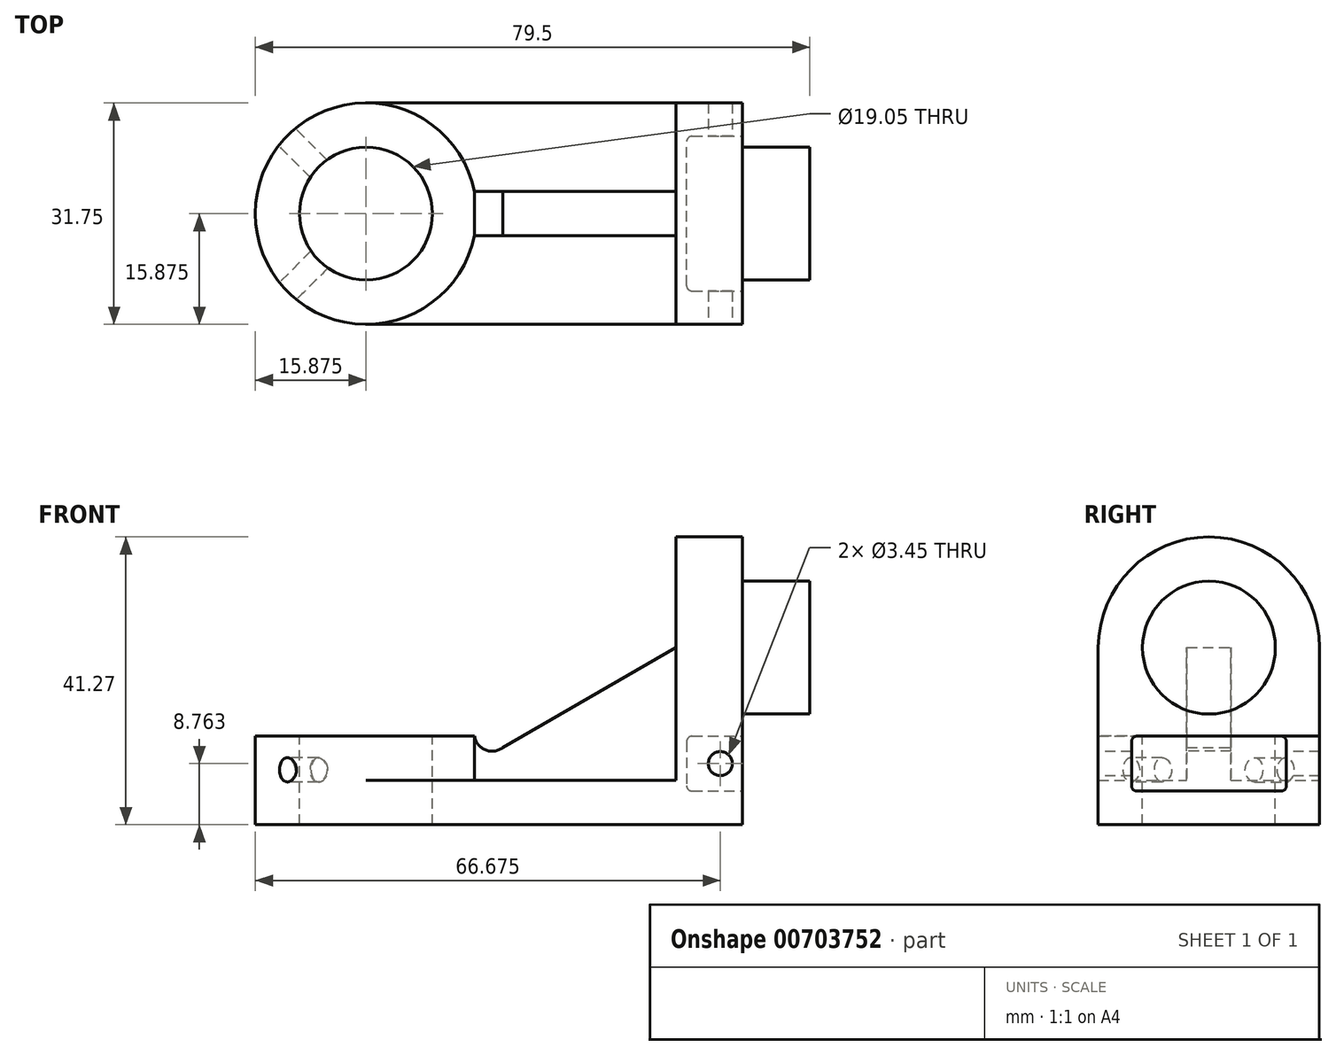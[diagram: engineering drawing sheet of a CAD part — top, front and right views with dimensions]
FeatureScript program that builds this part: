
annotation { "Feature Type Name" : "Feature", "Feature Type Description" : "" }
export const myFeature = defineFeature(function(context is Context, id is Id, definition is map)
    precondition{}
    {
        {
            var Q0;
            Q0=qCreatedBy(makeId("Top.planeOp"),FACE);
            var sketch = newSketch(context, id + "F0", { "sketchPlane" : qUnion([Q0])});
            skLineSegment(sketch, "E0.bottom", {"start": v(0, 0) * mm, "end": v(-53.98, 0) * mm});
            skLineSegment(sketch, "E0.top", {"start": v(0, -31.75) * mm, "end": v(-53.97, -31.75) * mm});
            skLineSegment(sketch, "E0.left", {"start": v(0, 0) * mm, "end": v(0, -31.75) * mm});
            skLineSegment(sketch, "E0.right", {"start": v(-53.98, 0) * mm, "end": v(-53.97, -31.75) * mm});
            skSolve(sketch);
        }
        {
            var Q0;
            Q0 = qSketchRegion(id + "F0", true);
            extrude(context, id + "F1", {"entities" : qUnion([Q0]), "depth" : 6.35 * mm, "offsetDistance" : 25.4 * mm});
        }
        {
            var Q0;
            Q0=makeQuery(id+"F1.opExtrude","CAP_FACE",FACE,{"disambiguationData":[OSD([sQuery(id+"F0.wireOp",EDGE,"E0.bottom"),sQuery(id+"F0.wireOp",EDGE,"E0.top"),sQuery(id+"F0.wireOp",EDGE,"E0.left"),sQuery(id+"F0.wireOp",EDGE,"E0.right")])],"isStart":false});
            var sketch = newSketch(context, id + "F2", { "sketchPlane" : qUnion([Q0])});
            skCircle(sketch, "E1", {"center": v(-53.98, -15.88) * mm, "radius": 15.88 * mm});
            skSolve(sketch);
        }
        {
            var Q0;
            Q0 = qSketchRegion(id + "F2", true);
            extrude(context, id + "F3", {"entities" : qUnion([Q0]), "operationType" : NewBodyOperationType.ADD, "depth" : 6.35 * mm, "offsetDistance" : 25.4 * mm, "hasSecondDirection" : true, "secondDirectionOppositeDirection" : true, "secondDirectionDepth" : 6.35 * mm});
        }
        {
            var Q0;
            Q0=makeQuery(id+"F3.opExtrude","CAP_FACE",FACE,{"disambiguationData":[OSD([sQuery(id+"F2.wireOp",EDGE,"E1")])],"isStart":false});
            var sketch = newSketch(context, id + "F4", { "sketchPlane" : qUnion([Q0])});
            skCircle(sketch, "E2", {"center": v(-53.98, -15.88) * mm, "radius": 9.53 * mm});
            skSolve(sketch);
        }
        {
            var Q0;
            Q0 = qSketchRegion(id + "F4", true);
            extrude(context, id + "F5", {"entities" : qUnion([Q0]), "operationType" : NewBodyOperationType.REMOVE, "oppositeDirection" : true, "depth" : 25.4 * mm, "offsetDistance" : 25.4 * mm});
        }
        {
            var Q0;
            Q0=makeQuery(id+"F1.opExtrude","SWEPT_FACE",FACE,{"disambiguationData":[OSD([sQuery(id+"F0.wireOp",EDGE,"E0.left")])]});
            var sketch = newSketch(context, id + "F6", { "sketchPlane" : qUnion([Q0])});
            skCircle(sketch, "E3", {"center": v(-15.88, 25.4) * mm, "radius": 9.53 * mm});
            skPoint(sketch, "E3.centerSnap0", {"position": v(-15.88, 6.35) * mm});
            skCircle(sketch, "E4", {"center": v(-15.88, 25.4) * mm, "radius": 15.88 * mm});
            skLineSegment(sketch, "E5", {"start": v(0, 0) * mm, "end": v(0, 25.4) * mm});
            skPoint(sketch, "E5.endSnap0", {"position": v(0, 3.18) * mm});
            skLineSegment(sketch, "E6", {"start": v(-31.75, 0) * mm, "end": v(-31.75, 25.4) * mm});
            skLineSegment(sketch, "E7", {"start": v(-31.75, 0) * mm, "end": v(0, 0) * mm});
            skSolve(sketch);
        }
        {
            var Q0;
            {var subQ5=makeQuery(id+"F1.opExtrude","CAP_EDGE",EDGE,{"disambiguationData":[OSD([sQuery(id+"F0.wireOp",EDGE,"E0.left")])],"isStart":false});Q0=makeQuery(id+"F6.imprint","IMPRINT",FACE,{"disambiguationData":[TD([[makeQuery(id+"F6.imprint","IMPRINT",EDGE,{"derivedFrom":subQ5}),-1.0]])]});}
            var Q1;
            {var subQ0=sQuery(id+"F6.wireOp",EDGE,"E7");Q1=makeQuery(id+"F6.imprint","IMPRINT",FACE,{"disambiguationData":[TD([[makeQuery(id+"F6.imprint","IMPRINT",EDGE,{"derivedFrom":subQ0}),-1.0]])]});}
            var Q2;
            Q2=makeQuery(id+"F6.imprint","IMPRINT",FACE,{"disambiguationData":[TD([[makeQuery(id+"F6.imprint","IMPRINT",EDGE,{"derivedFrom":sQuery(id+"F6.wireOp",EDGE,"E3")}),-1.0]])]});
            extrude(context, id + "F7", {"entities" : qUnion([Q0, Q1, Q2]), "operationType" : NewBodyOperationType.ADD, "oppositeDirection" : true, "depth" : 9.52 * mm, "offsetDistance" : 25.4 * mm});
        }
        {
            var Q0;
            Q0=makeQuery(id+"F7.boolean.opBoolean","MERGE",FACE,{"derivedFrom":[makeQuery(id+"F1.opExtrude","SWEPT_FACE",FACE,{"disambiguationData":[OSD([sQuery(id+"F0.wireOp",EDGE,"E0.left")])]}),makeQuery(id+"F7.opExtrude","CAP_FACE",FACE,{"disambiguationData":[OSD([sQuery(id+"F6.wireOp",EDGE,"E3"),sQuery(id+"F6.wireOp",EDGE,"E4"),sQuery(id+"F6.wireOp",EDGE,"E5"),sQuery(id+"F6.wireOp",EDGE,"E6"),sQuery(id+"F6.wireOp",EDGE,"E7")])],"isStart":true})]});
            var sketch = newSketch(context, id + "F8", { "sketchPlane" : qUnion([Q0])});
            skCircle(sketch, "E8", {"center": v(-15.88, 25.4) * mm, "radius": 9.53 * mm});
            skSolve(sketch);
        }
        {
            var Q0;
            Q0=makeQuery(id+"F8.imprint","IMPRINT",FACE,{"disambiguationData":[TD([[makeQuery(id+"F8.imprint","IMPRINT",EDGE,{"derivedFrom":sQuery(id+"F8.wireOp",EDGE,"E8")}),1.0]])]});
            extrude(context, id + "F9", {"entities" : qUnion([Q0]), "operationType" : NewBodyOperationType.ADD, "depth" : 9.65 * mm, "offsetDistance" : 25.4 * mm, "hasSecondDirection" : true, "secondDirectionOppositeDirection" : true, "secondDirectionDepth" : 9.52 * mm});
        }
        {
            var Q0;
            Q0=qCreatedBy(makeId("Front.planeOp"),FACE);
            cPlane(context, id + "F10", {"entities" : qUnion([Q0]), "cplaneType" : CPlaneType.OFFSET, "offset" : 15.88 * mm, "width" : 152.4 * mm, "height" : 152.4 * mm});
        }
        {
            var Q0;
            Q0=qCreatedBy(id+"F10.planeOp",FACE);
            var sketch = newSketch(context, id + "F11", { "sketchPlane" : qUnion([Q0])});
            skLineSegment(sketch, "E9", {"start": v(-9.52, 25.4) * mm, "end": v(-34.38, 11.05) * mm});
            skLineSegment(sketch, "E10", {"start": v(-34.38, 11.05) * mm, "end": v(-34.38, 12.7) * mm});
            skLineSegment(sketch, "E11", {"start": v(-34.38, 12.7) * mm, "end": v(-38.95, 12.7) * mm});
            skLineSegment(sketch, "E12", {"start": v(-38.95, 12.7) * mm, "end": v(-38.95, 6.35) * mm});
            skLineSegment(sketch, "E13", {"start": v(-38.95, 6.35) * mm, "end": v(-9.52, 6.35) * mm});
            skLineSegment(sketch, "E14", {"start": v(-9.52, 6.35) * mm, "end": v(-9.53, 25.4) * mm});
            skSolve(sketch);
        }
        {
            var Q0;
            Q0 = qSketchRegion(id + "F11", true);
            extrude(context, id + "F12", {"entities" : qUnion([Q0]), "operationType" : NewBodyOperationType.ADD, "endBound" : BoundingType.SYMMETRIC, "depth" : 6.35 * mm, "offsetDistance" : 25.4 * mm});
        }
        {
            var Q0;
            Q0=makeQuery(id+"F12.opExtrude","CAP_FACE",FACE,{"disambiguationData":[OSD([sQuery(id+"F11.wireOp",EDGE,"E9"),sQuery(id+"F11.wireOp",EDGE,"E10"),sQuery(id+"F11.wireOp",EDGE,"E11"),sQuery(id+"F11.wireOp",EDGE,"E12"),sQuery(id+"F11.wireOp",EDGE,"E13"),sQuery(id+"F11.wireOp",EDGE,"E14")])],"isStart":false});
            var sketch = newSketch(context, id + "F13", { "sketchPlane" : qUnion([Q0])});
            skCircle(sketch, "E15", {"center": v(-35.9, 13.08) * mm, "radius": 2.54 * mm});
            skPoint(sketch, "E15.first.point", {"position": v(-34.38, 11.05) * mm});
            skPoint(sketch, "E15.second.point", {"position": v(-38.42, 12.7) * mm});
            skPoint(sketch, "E15.third.point", {"position": v(-35.8, 15.62) * mm});
            skSolve(sketch);
        }
        {
            var Q0;
            Q0 = qSketchRegion(id + "F13", true);
            extrude(context, id + "F14", {"entities" : qUnion([Q0]), "operationType" : NewBodyOperationType.REMOVE, "endBound" : BoundingType.THROUGH_ALL, "oppositeDirection" : true, "depth" : 25.4 * mm, "offsetDistance" : 25.4 * mm});
        }
        {
            var Q0;
            Q0=makeQuery(id+"F7.boolean.opBoolean","MERGE",FACE,{"derivedFrom":[makeQuery(id+"F1.opExtrude","SWEPT_FACE",FACE,{"disambiguationData":[OSD([sQuery(id+"F0.wireOp",EDGE,"E0.top")])]}),makeQuery(id+"F7.opExtrude","SWEPT_FACE",FACE,{"disambiguationData":[OSD([sQuery(id+"F6.wireOp",EDGE,"E6")])]})]});
            var sketch = newSketch(context, id + "F15", { "sketchPlane" : qUnion([Q0])});
            skCircle(sketch, "E16", {"center": v(-3.18, 8.76) * mm, "radius": 1.73 * mm});
            skSolve(sketch);
        }
        {
            var Q0;
            Q0 = qSketchRegion(id + "F15", true);
            extrude(context, id + "F16", {"entities" : qUnion([Q0]), "operationType" : NewBodyOperationType.REMOVE, "endBound" : BoundingType.THROUGH_ALL, "oppositeDirection" : true, "depth" : 25.4 * mm, "offsetDistance" : 25.4 * mm});
        }
        {
            var Q0;
            Q0=makeQuery(id+"F7.boolean.opBoolean","MERGE",FACE,{"derivedFrom":[makeQuery(id+"F1.opExtrude","SWEPT_FACE",FACE,{"disambiguationData":[OSD([sQuery(id+"F0.wireOp",EDGE,"E0.left")])]}),makeQuery(id+"F7.opExtrude","CAP_FACE",FACE,{"disambiguationData":[OSD([sQuery(id+"F6.wireOp",EDGE,"E3"),sQuery(id+"F6.wireOp",EDGE,"E4"),sQuery(id+"F6.wireOp",EDGE,"E5"),sQuery(id+"F6.wireOp",EDGE,"E6"),sQuery(id+"F6.wireOp",EDGE,"E7")])],"isStart":true})]});
            var sketch = newSketch(context, id + "F17", { "sketchPlane" : qUnion([Q0])});
            skLineSegment(sketch, "E17.bottom", {"start": v(-26.97, 12.7) * mm, "end": v(-4.78, 12.7) * mm});
            skLineSegment(sketch, "E17.top", {"start": v(-26.97, 4.83) * mm, "end": v(-4.78, 4.83) * mm});
            skLineSegment(sketch, "E17.left", {"start": v(-26.97, 12.7) * mm, "end": v(-26.97, 4.83) * mm});
            skLineSegment(sketch, "E17.right", {"start": v(-4.78, 12.7) * mm, "end": v(-4.78, 4.83) * mm});
            skSolve(sketch);
        }
        {
            var Q0;
            Q0=makeQuery(id+"F17.imprint","IMPRINT",FACE,{"disambiguationData":[TD([[makeQuery(id+"F17.imprint","IMPRINT",EDGE,{"derivedFrom":sQuery(id+"F17.wireOp",EDGE,"E17.bottom")}),-1.0]])]});
            extrude(context, id + "F18", {"entities" : qUnion([Q0]), "operationType" : NewBodyOperationType.REMOVE, "oppositeDirection" : true, "depth" : 8 * mm, "offsetDistance" : 25.4 * mm});
        }
        {
            var Q0;
            Q0=makeQuery(id+"F18.boolean.opBoolean","COPY",EDGE,{"derivedFrom":makeQuery(id+"F18.opExtrude","SWEPT_EDGE",EDGE,{"disambiguationData":[OSD([sQuery(id+"F17.wireOp",EDGE,"E17.top"),sQuery(id+"F17.wireOp",EDGE,"E17.right")])]})});
            var Q1;
            Q1=makeQuery(id+"F18.boolean.opBoolean","COPY",EDGE,{"derivedFrom":makeQuery(id+"F18.opExtrude","CAP_EDGE",EDGE,{"disambiguationData":[OSD([sQuery(id+"F17.wireOp",EDGE,"E17.top")])],"isStart":false})});
            var Q2;
            Q2=makeQuery(id+"F18.boolean.opBoolean","COPY",EDGE,{"derivedFrom":makeQuery(id+"F18.opExtrude","SWEPT_EDGE",EDGE,{"disambiguationData":[OSD([sQuery(id+"F17.wireOp",EDGE,"E17.top"),sQuery(id+"F17.wireOp",EDGE,"E17.left")])]})});
            var Q3;
            Q3=makeQuery(id+"F18.boolean.opBoolean","COPY",EDGE,{"derivedFrom":makeQuery(id+"F18.opExtrude","CAP_EDGE",EDGE,{"disambiguationData":[OSD([sQuery(id+"F17.wireOp",EDGE,"E17.bottom")])],"isStart":false})});
            var Q4;
            Q4=makeQuery(id+"F18.boolean.opBoolean","COPY",EDGE,{"derivedFrom":makeQuery(id+"F18.opExtrude","SWEPT_EDGE",EDGE,{"disambiguationData":[OSD([sQuery(id+"F17.wireOp",EDGE,"E17.bottom"),sQuery(id+"F17.wireOp",EDGE,"E17.right")])]})});
            var Q5;
            Q5=makeQuery(id+"F18.boolean.opBoolean","COPY",EDGE,{"derivedFrom":makeQuery(id+"F18.opExtrude","SWEPT_EDGE",EDGE,{"disambiguationData":[OSD([sQuery(id+"F17.wireOp",EDGE,"E17.bottom"),sQuery(id+"F17.wireOp",EDGE,"E17.left")])]})});
            var Q6;
            Q6=makeQuery(id+"F18.boolean.opBoolean","COPY",EDGE,{"derivedFrom":makeQuery(id+"F18.opExtrude","CAP_EDGE",EDGE,{"disambiguationData":[OSD([sQuery(id+"F17.wireOp",EDGE,"E17.left")])],"isStart":false})});
            var Q7;
            Q7=makeQuery(id+"F18.boolean.opBoolean","COPY",EDGE,{"derivedFrom":makeQuery(id+"F18.opExtrude","CAP_EDGE",EDGE,{"disambiguationData":[OSD([sQuery(id+"F17.wireOp",EDGE,"E17.right")])],"isStart":false})});
            var Q8;
            Q8=makeQuery(id+"F12.opExtrude","CAP_EDGE",EDGE,{"disambiguationData":[OSD([sQuery(id+"F11.wireOp",EDGE,"E14")])],"isStart":false});
            var Q9;
            Q9=makeQuery(id+"F12.opExtrude","CAP_EDGE",EDGE,{"disambiguationData":[OSD([sQuery(id+"F11.wireOp",EDGE,"E14")])],"isStart":true});
            fillet(context, id + "F19", {"entities" : qUnion([Q0, Q1, Q2, Q3, Q4, Q5, Q6, Q7, Q8, Q9]), "radius" : 0.76 * mm, "tangentPropagation" : true, "allowEdgeOverflow" : false});
        }
        {
            var Q0;
            Q0=makeQuery(id+"F12.boolean.opBoolean","MERGE",FACE,{"derivedFrom":[makeQuery(id+"F3.opExtrude","CAP_FACE",FACE,{"disambiguationData":[OSD([sQuery(id+"F2.wireOp",EDGE,"E1")])],"isStart":false}),makeQuery(id+"F12.opExtrude","SWEPT_FACE",FACE,{"disambiguationData":[OSD([sQuery(id+"F11.wireOp",EDGE,"E11")])]})]});
            var sketch = newSketch(context, id + "F20", { "sketchPlane" : qUnion([Q0])});
            skPoint(sketch, "E18.startSnap0", {"position": v(-38.42, -15.88) * mm});
            skLineSegment(sketch, "E19", {"start": v(-53.98, -15.88) * mm, "end": v(-53.98, 11.66) * mm, "construction": true});
            skLineSegment(sketch, "E20", {"start": v(-53.98, -15.88) * mm, "end": v(-53.98, -43.2) * mm, "construction": true});
            skLineSegment(sketch, "E21", {"start": v(-53.98, -15.88) * mm, "end": v(-69.85, -31.75) * mm, "construction": true});
            skPoint(sketch, "E21.endSnap0", {"position": v(-69.85, -15.88) * mm});
            skLineSegment(sketch, "E22", {"start": v(-53.97, -15.88) * mm, "end": v(-73.43, 3.58) * mm, "construction": true});
            skSolve(sketch);
        }
        {
            var Q0;
            Q0=sQuery(id+"F20.wireOp",EDGE,"E21");
            cPlane(context, id + "F21", {"entities" : qUnion([Q0]), "cplaneType" : CPlaneType.MID_PLANE, "offset" : 25.4 * mm, "width" : 152.4 * mm, "height" : 152.4 * mm});
        }
        {
            var Q0;
            Q0=sQuery(id+"F20.wireOp",EDGE,"E22");
            cPlane(context, id + "F22", {"entities" : qUnion([Q0]), "cplaneType" : CPlaneType.MID_PLANE, "offset" : 25.4 * mm, "width" : 152.4 * mm, "height" : 152.4 * mm});
        }
        {
            var Q0;
            Q0=qCreatedBy(id+"F21.planeOp",FACE);
            cPlane(context, id + "F23", {"entities" : qUnion([Q0]), "cplaneType" : CPlaneType.OFFSET, "offset" : 6.35 * mm, "width" : 152.4 * mm, "height" : 152.4 * mm});
        }
        {
            var Q0;
            Q0=qCreatedBy(id+"F23.planeOp",FACE);
            var sketch = newSketch(context, id + "F24", { "sketchPlane" : qUnion([Q0])});
            skCircle(sketch, "E23", {"center": v(-27, 7.87) * mm, "radius": 1.73 * mm});
            skSolve(sketch);
        }
        {
            var Q0;
            Q0=makeQuery(id+"F24.imprint","IMPRINT",FACE,{"disambiguationData":[TD([[makeQuery(id+"F24.imprint","IMPRINT",EDGE,{"derivedFrom":sQuery(id+"F24.wireOp",EDGE,"E23")}),1.0]])]});
            extrude(context, id + "F25", {"entities" : qUnion([Q0]), "operationType" : NewBodyOperationType.REMOVE, "oppositeDirection" : true, "depth" : 12.7 * mm, "offsetDistance" : 25.4 * mm});
        }
        {
            var Q0;
            Q0=qCreatedBy(id+"F22.planeOp",FACE);
            cPlane(context, id + "F26", {"entities" : qUnion([Q0]), "cplaneType" : CPlaneType.OFFSET, "offset" : 3.8 * mm, "width" : 152.4 * mm, "height" : 152.4 * mm});
        }
        {
            var Q0;
            Q0=qCreatedBy(id+"F26.planeOp",FACE);
            var sketch = newSketch(context, id + "F27", { "sketchPlane" : qUnion([Q0])});
            skCircle(sketch, "E24", {"center": v(49.63, 7.87) * mm, "radius": 1.73 * mm});
            skSolve(sketch);
        }
        {
            var Q0;
            Q0 = qSketchRegion(id + "F27", true);
            extrude(context, id + "F28", {"entities" : qUnion([Q0]), "operationType" : NewBodyOperationType.REMOVE, "oppositeDirection" : true, "depth" : 12.7 * mm, "offsetDistance" : 25.4 * mm});
        }
    });
